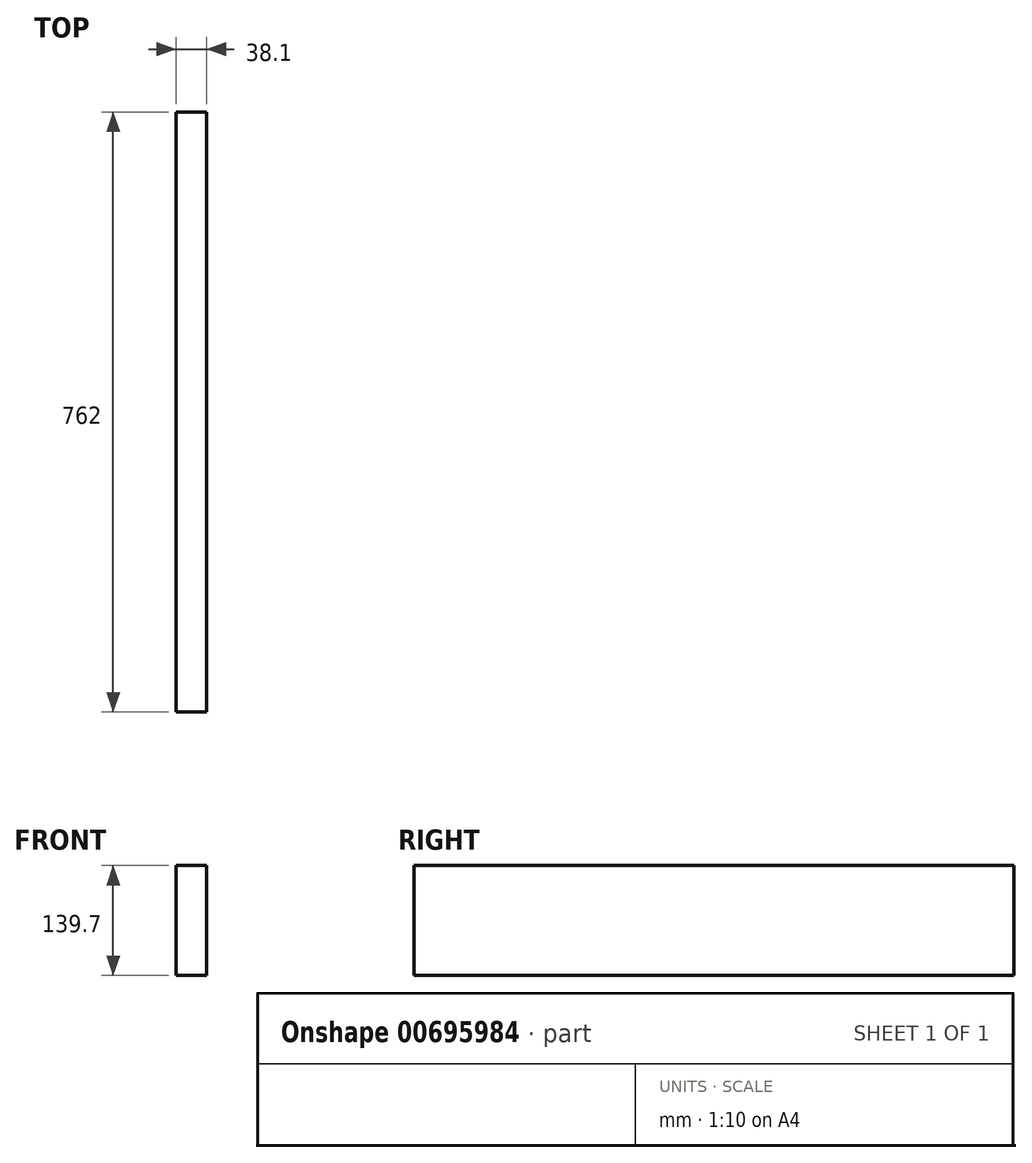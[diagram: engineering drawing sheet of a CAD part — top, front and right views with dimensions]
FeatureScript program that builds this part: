
annotation { "Feature Type Name" : "Feature", "Feature Type Description" : "" }
export const myFeature = defineFeature(function(context is Context, id is Id, definition is map)
    precondition{}
    {
        {
            var Q0;
            Q0=qCreatedBy(makeId("Right.planeOp"),FACE);
            var sketch = newSketch(context, id + "F0", { "sketchPlane" : qUnion([Q0])});
            skLineSegment(sketch, "E0.bottom", {"start": v(0, 0) * mm, "end": v(-762, 0) * mm});
            skLineSegment(sketch, "E0.top", {"start": v(0, 139.7) * mm, "end": v(-762, 139.7) * mm});
            skLineSegment(sketch, "E0.left", {"start": v(0, 0) * mm, "end": v(0, 139.7) * mm});
            skLineSegment(sketch, "E0.right", {"start": v(-762, 0) * mm, "end": v(-762, 139.7) * mm});
            skSolve(sketch);
        }
        {
            var Q0;
            Q0 = qSketchRegion(id + "F0", true);
            extrude(context, id + "F1", {"entities" : qUnion([Q0]), "depth" : 38.1 * mm, "offsetDistance" : 25.4 * mm});
        }
    });
